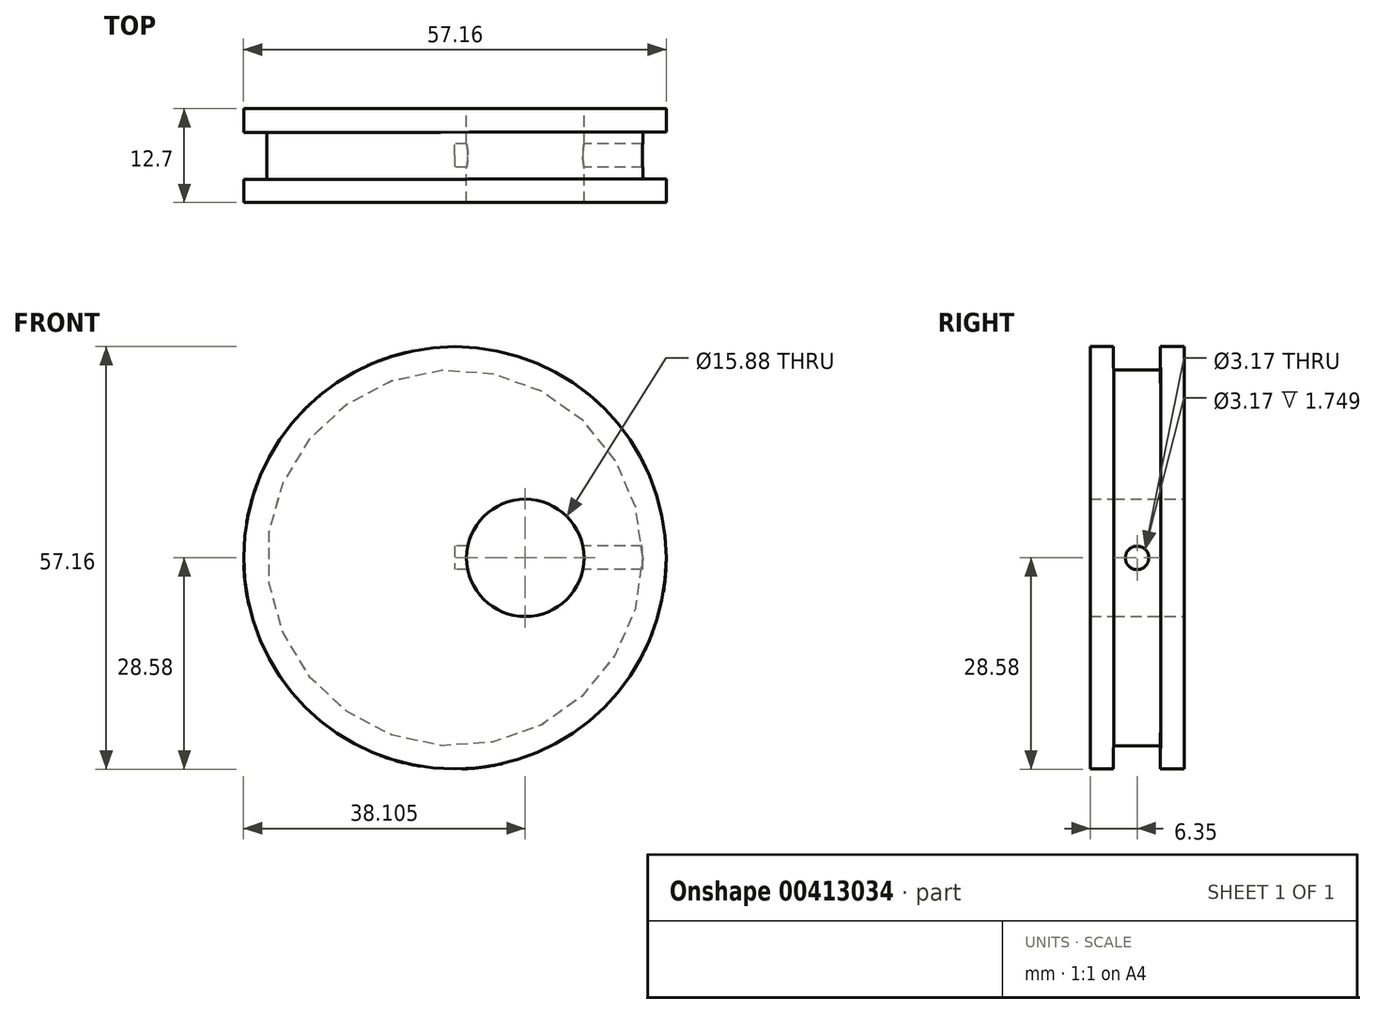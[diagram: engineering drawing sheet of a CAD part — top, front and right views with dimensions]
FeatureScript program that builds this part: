
annotation { "Feature Type Name" : "Feature", "Feature Type Description" : "" }
export const myFeature = defineFeature(function(context is Context, id is Id, definition is map)
    precondition{}
    {
        {
            var Q0;
            Q0=qCreatedBy(makeId("Front.planeOp"),FACE);
            var sketch = newSketch(context, id + "F0", { "sketchPlane" : qUnion([Q0])});
            skCircle(sketch, "E0", {"center": v(0, 0) * mm, "radius": 28.58 * mm});
            skCircle(sketch, "E1", {"center": v(9.53, 0) * mm, "radius": 7.94 * mm});
            skSolve(sketch);
        }
        {
            var Q0;
            Q0=makeQuery(id+"F0.imprint","IMPRINT",FACE,{"disambiguationData":[TD([[makeQuery(id+"F0.imprint","IMPRINT",EDGE,{"derivedFrom":sQuery(id+"F0.wireOp",EDGE,"E0")}),1.0]])]});
            extrude(context, id + "F1", {"entities" : qUnion([Q0]), "depth" : 12.7 * mm});
        }
        {
            var Q0;
            Q0=qCreatedBy(makeId("Top.planeOp"),FACE);
            var sketch = newSketch(context, id + "F2", { "sketchPlane" : qUnion([Q0])});
            skLineSegment(sketch, "E2.bottom", {"start": v(28.58, -3.18) * mm, "end": v(25.4, -3.18) * mm});
            skLineSegment(sketch, "E2.top", {"start": v(28.58, -9.53) * mm, "end": v(25.4, -9.53) * mm});
            skLineSegment(sketch, "E2.left", {"start": v(28.58, -3.18) * mm, "end": v(28.58, -9.53) * mm});
            skLineSegment(sketch, "E2.right", {"start": v(25.4, -3.18) * mm, "end": v(25.4, -9.53) * mm});
            skSolve(sketch);
        }
        {
            var Q0;
            Q0=qCreatedBy(makeId("Top.planeOp"),FACE);
            var sketch = newSketch(context, id + "F3", { "sketchPlane" : qUnion([Q0])});
            skLineSegment(sketch, "E3", {"start": v(0, 3.89) * mm, "end": v(0, -14.52) * mm});
            skSolve(sketch);
        }
        {
            var Q0;
            Q0 = qSketchRegion(id + "F2", true);
            var Q1;
            Q1=sQuery(id+"F3.wireOp",EDGE,"E3");
            revolve(context, id + "F4", {"operationType" : NewBodyOperationType.REMOVE, "entities" : qUnion([Q0]), "axis" : qUnion([Q1]), "revolveType" : RevolveType.FULL, "oppositeDirection" : true});
        }
        {
            var Q0;
            Q0=qCreatedBy(makeId("Right.planeOp"),FACE);
            var sketch = newSketch(context, id + "F5", { "sketchPlane" : qUnion([Q0])});
            skCircle(sketch, "E4", {"center": v(-6.35, 0) * mm, "radius": 1.59 * mm});
            skSolve(sketch);
        }
        {
            var Q0;
            Q0 = qSketchRegion(id + "F5", true);
            extrude(context, id + "F6", {"entities" : qUnion([Q0]), "operationType" : NewBodyOperationType.REMOVE, "depth" : 25.4 * mm});
        }
    });
